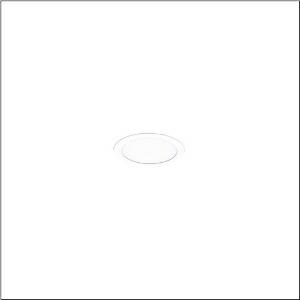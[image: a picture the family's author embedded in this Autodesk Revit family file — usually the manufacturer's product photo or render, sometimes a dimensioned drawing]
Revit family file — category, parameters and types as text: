
# Revit family: lunis_21_s_51db16ta91c
name_source: partatom
category: Lighting Fixtures
units: mm (PartAtom-declared; Revit-internal decimal feet)

## family parameters
Cut with Voids When Loaded = No
Host = Face
Light Source = No
Part Type = Normal
Room Calculation Point = No
Round Connector Dimension = Use Diameter
Shared = No

## types (1)
- --- (1 x LED 3000 K ... 6500 K, 1010 lm, 8 W, 4000K)
    Apparent Load = 8 VA
    CIE Flux Codes = 50 80 96 100 100
    Color Rendering = 80
    Color Temperature = 4000K
    Default Elevation = 1800 mm
    Description = Lunis 21,  S, downlight, light control with lens, of PMMA, optical cover: cover panel, of PC, opal, light emission: direct distribution, LED rated luminous flux: 1.010lm, light colour: 8tw, with terminal, 5-pole, mains connection: 220..240V, AC, 50..60Hz, housing, round, of diecast aluminium, traffic white (RAL 9016), diameter: 84mm, clamping range: 1..40mm, protection rating (complete): IP20, protection rating (on room side): IP54, insulation class (complete): insulation class II (safety insulation), certification: CE, impact resistance: IK03, packaging unit: 1 piece
    Height = 0 mm  [stored 0 ft]
    Lamp = 1 x LED 3000 K ... 6500 K
    Lamp Light Flux = 1010 lm
    Lamp Power = 8 W
    Lamp count = 1
    Length = 84 mm
    Luminous efficacy = 126 lm/W
    Manufacturer = Siteco
    ModVariant = No
    Model = 51DB16TA91C
    Mounting Place = Ceiling
    Mounting Type = Recessed
    Number of Poles = 1
    OnlyDefault = Yes
    Power Factor = 1
    Product Name = Lunis 21 S
    Product group = downlight
    ProductGroupID = 400
    Protection Class = Protection class II
    Protection Degree = IP 20
    RLX_Detail_Level = 1
    RLX_Emergency_Light_Flux = 0 lm
    RLX_Emergency_Type = 0
    RLX_Emergency_Type_DB = No
    RlxData = <blob elided: 7801 chars, md5=94fe6847>
    Socket = socket
    Standby Power = 0 W
    System Light Flux = 1010 lm
    System Power = 8 W
    Type Comments = individual setting: CCT=4000K, colour temperature 4000K, luminous flux: 100 % | (OFF | OFF | ON | OFF) | 200 mA
    Type Image = l_1290838.jpg
    URL = http://relux.com
    VarID = @adj_018586
    Voltage = 0 V
    Weight = 0.00 kg
    Width = 0 mm  [stored 0 ft]

note: [stored X ft] marks values corroborated as IEEE doubles in the binary element streams (Revit-internal decimal feet)

## geometry (parser evidence)
native form markers: Sweep x7
no freeform markers — native parametric forms only
